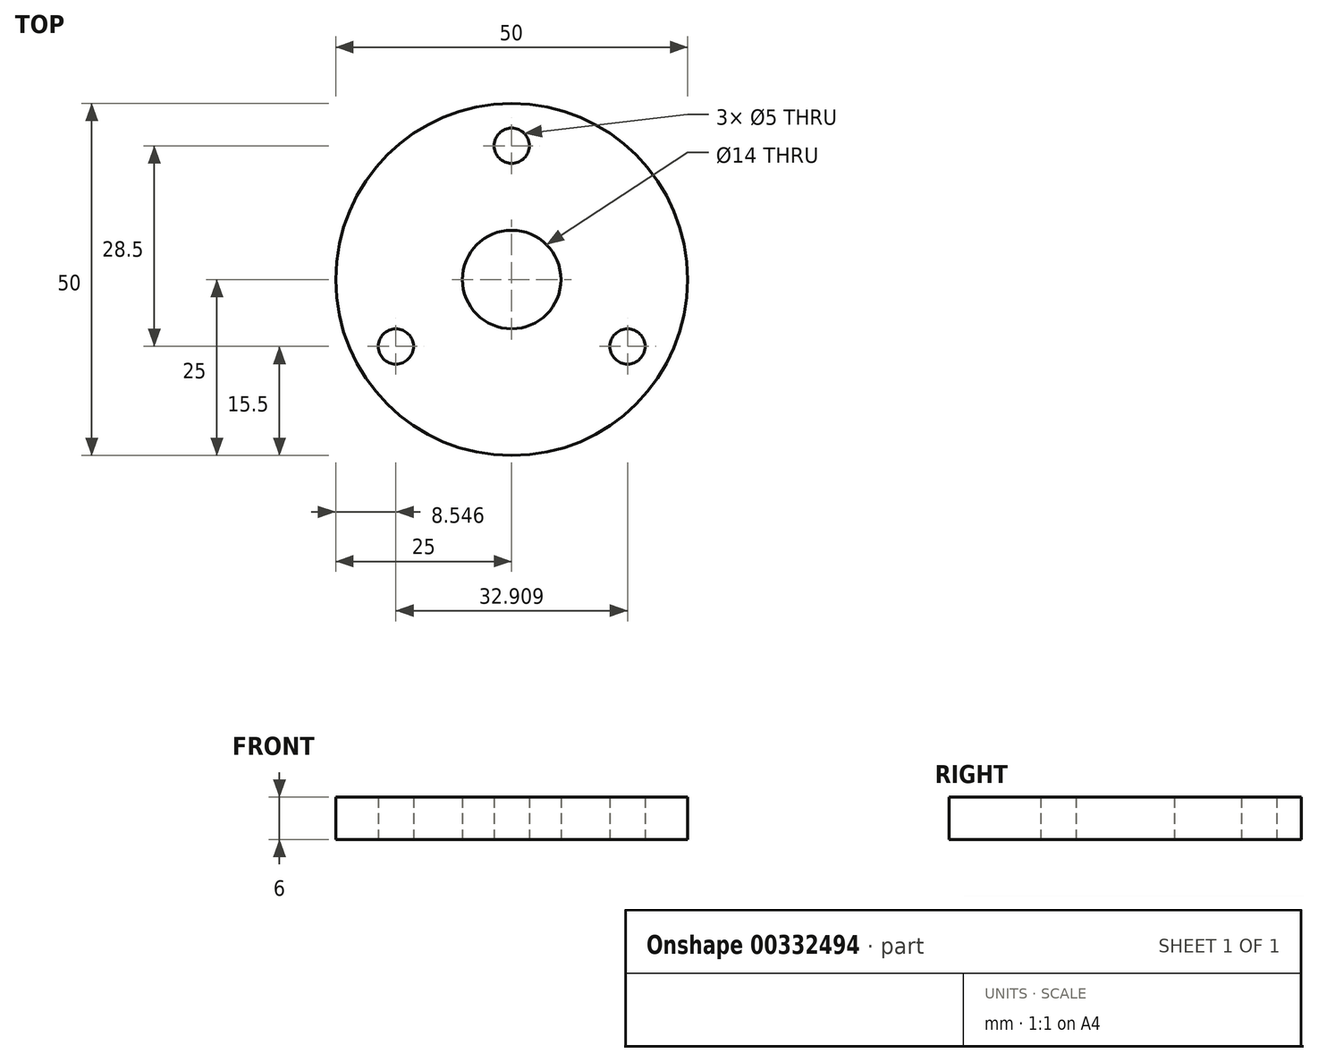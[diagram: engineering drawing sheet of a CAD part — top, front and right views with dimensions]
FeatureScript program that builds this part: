
annotation { "Feature Type Name" : "Feature", "Feature Type Description" : "" }
export const myFeature = defineFeature(function(context is Context, id is Id, definition is map)
    precondition{}
    {
        {
            var Q0;
            Q0=qCreatedBy(makeId("Top.planeOp"),FACE);
            var sketch = newSketch(context, id + "F0", { "sketchPlane" : qUnion([Q0])});
            skCircle(sketch, "E0", {"center": v(0, 0) * mm, "radius": 25 * mm});
            skCircle(sketch, "E1", {"center": v(0, 19) * mm, "radius": 2.5 * mm});
            skCircle(sketch, "E2", {"center": v(-16.45, -9.5) * mm, "radius": 2.5 * mm});
            skCircle(sketch, "E3", {"center": v(16.45, -9.5) * mm, "radius": 2.5 * mm});
            skSolve(sketch);
        }
        {
            var Q0;
            Q0 = qSketchRegion(id + "F0", true);
            extrude(context, id + "F1", {"entities" : qUnion([Q0]), "depth" : 6 * mm});
        }
        {
            var Q0;
            Q0=qCreatedBy(makeId("Top.planeOp"),FACE);
            var sketch = newSketch(context, id + "F2", { "sketchPlane" : qUnion([Q0])});
            skCircle(sketch, "E4", {"center": v(0, 0) * mm, "radius": 7 * mm});
            skSolve(sketch);
        }
        {
            var Q0;
            Q0=makeQuery(id+"F2.imprint","IMPRINT",FACE,{"disambiguationData":[TD([[makeQuery(id+"F2.imprint","IMPRINT",EDGE,{"derivedFrom":sQuery(id+"F2.wireOp",EDGE,"E4")}),1.0]])]});
            var Q1;
            Q1=sQuery(id+"F2.wireOp",EDGE,"E4");
            extrude(context, id + "F3", {"entities" : qUnion([Q0]), "operationType" : NewBodyOperationType.REMOVE, "surfaceEntities" : qUnion([Q1]), "depth" : 6 * mm});
        }
    });
